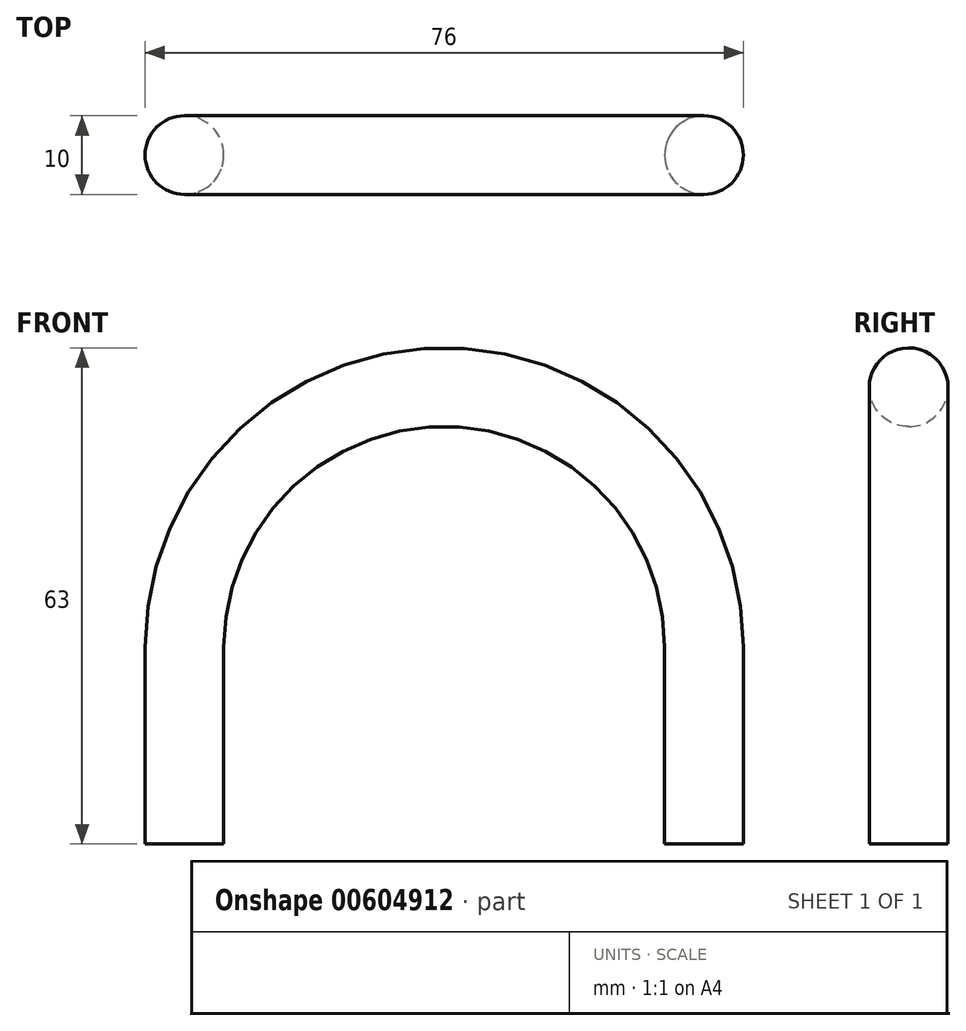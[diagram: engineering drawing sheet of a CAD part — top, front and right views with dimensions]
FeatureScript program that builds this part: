
annotation { "Feature Type Name" : "Feature", "Feature Type Description" : "" }
export const myFeature = defineFeature(function(context is Context, id is Id, definition is map)
    precondition{}
    {
        {
            var Q0;
            Q0=qCreatedBy(makeId("Front.planeOp"),FACE);
            var sketch = newSketch(context, id + "F0", { "sketchPlane" : qUnion([Q0])});
            skLineSegment(sketch, "E0", {"start": v(-35, 0) * mm, "end": v(-35, 25) * mm});
            skArc(sketch, "E1", {"start": v(-35, 25) * mm, "mid": v(0, 60) * mm, "end": v(35, 25) * mm});
            skLineSegment(sketch, "E2", {"start": v(35, 25) * mm, "end": v(35, 0) * mm});
            skLineSegment(sketch, "E3", {"start": v(0, 0) * mm, "end": v(0, 34.5) * mm, "construction": true});
            skSolve(sketch);
        }
        {
            var Q0;
            Q0=qCreatedBy(makeId("Top.planeOp"),FACE);
            var sketch = newSketch(context, id + "F1", { "sketchPlane" : qUnion([Q0])});
            skCircle(sketch, "E4", {"center": v(-33, 0) * mm, "radius": 5 * mm});
            skSolve(sketch);
        }
        {
            var Q0;
            Q0=makeQuery(id+"F1.imprint","IMPRINT",FACE,{"disambiguationData":[TD([[makeQuery(id+"F1.imprint","IMPRINT",EDGE,{"derivedFrom":sQuery(id+"F1.wireOp",EDGE,"E4")}),1.0]])]});
            var Q1;
            Q1 = qConstructionFilter(qBodyType(qCreatedBy(id + "F0" ,EDGE), BodyType.WIRE), ConstructionObject.NO);
            sweep(context, id + "F2", {"profiles" : qUnion([Q0]), "path" : qUnion([Q1])});
        }
    });
